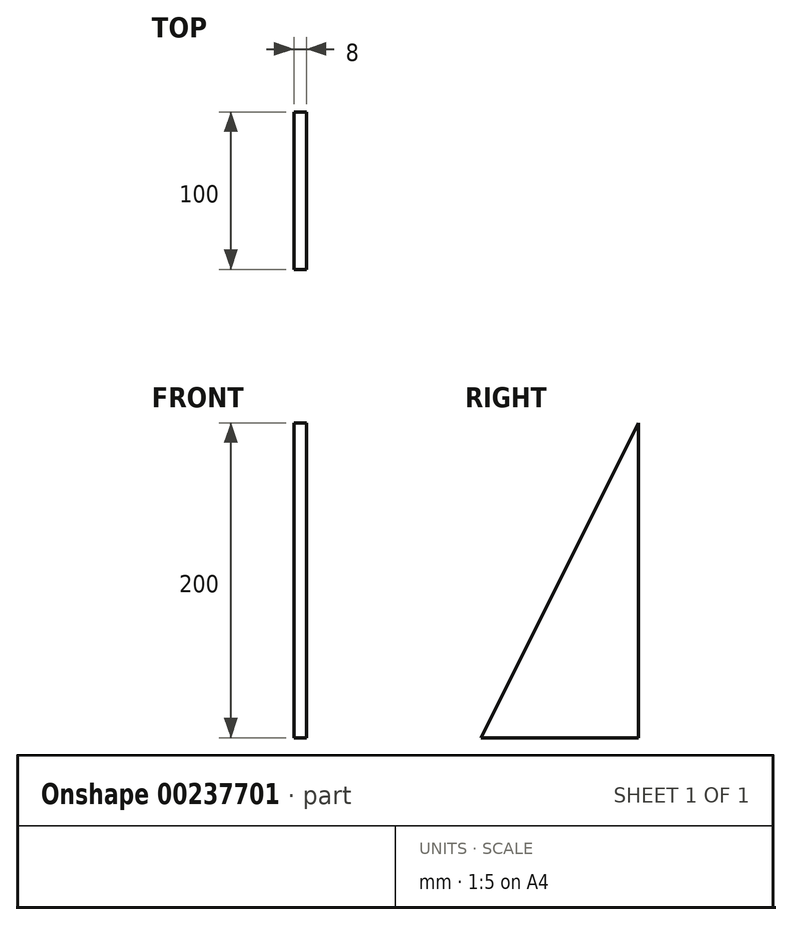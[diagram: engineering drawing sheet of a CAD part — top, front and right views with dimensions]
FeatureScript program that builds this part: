
annotation { "Feature Type Name" : "Feature", "Feature Type Description" : "" }
export const myFeature = defineFeature(function(context is Context, id is Id, definition is map)
    precondition{}
    {
        {
            var Q0;
            Q0=qCreatedBy(makeId("Right.planeOp"),FACE);
            var sketch = newSketch(context, id + "F0", { "sketchPlane" : qUnion([Q0])});
            skLineSegment(sketch, "E0.top", {"start": v(50, -100) * mm, "end": v(-50, -100) * mm});
            skLineSegment(sketch, "E0.left", {"start": v(50, 100) * mm, "end": v(50, -100) * mm});
            skPoint(sketch, "E0.middle", {"position": v(0, 0) * mm});
            skLineSegment(sketch, "E1", {"start": v(50, 100) * mm, "end": v(-50, -100) * mm});
            skPoint(sketch, "E0.right.start.orphan", {"position": v(-50, 100) * mm});
            skSolve(sketch);
        }
        {
            var Q0;
            Q0=makeQuery(id+"F0.imprint","IMPRINT",FACE,{"disambiguationData":[TD([[makeQuery(id+"F0.imprint","IMPRINT",EDGE,{"derivedFrom":sQuery(id+"F0.wireOp",EDGE,"E0.top")}),-1.0]])]});
            extrude(context, id + "F1", {"entities" : qUnion([Q0]), "depth" : 8 * mm});
        }
    });
